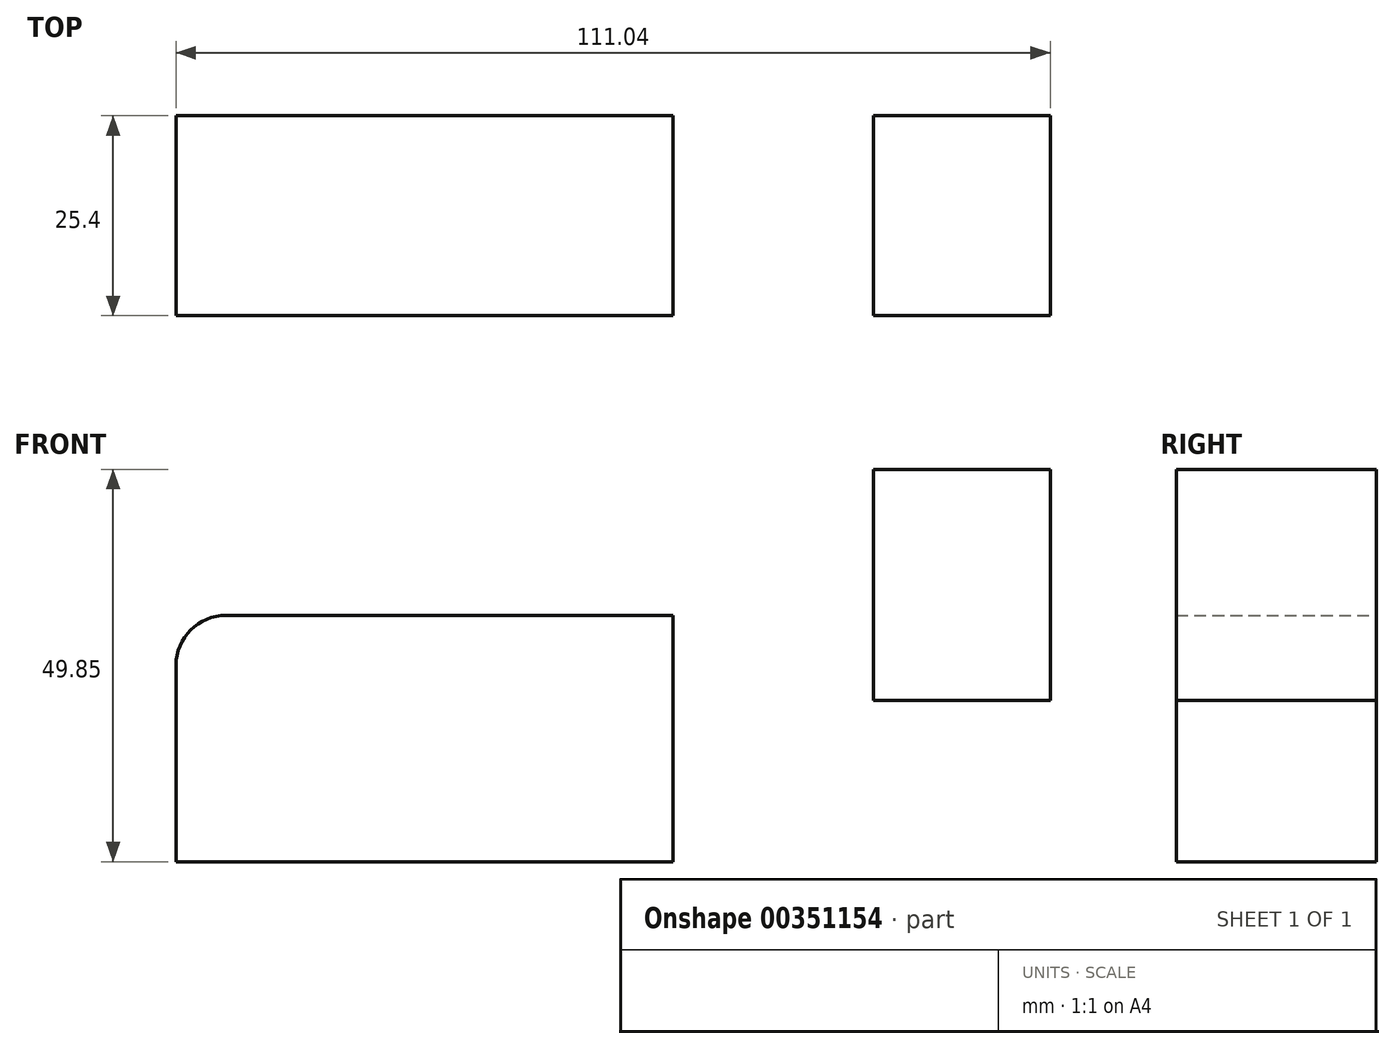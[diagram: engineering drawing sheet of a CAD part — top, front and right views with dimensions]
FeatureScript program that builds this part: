
annotation { "Feature Type Name" : "Feature", "Feature Type Description" : "" }
export const myFeature = defineFeature(function(context is Context, id is Id, definition is map)
    precondition{}
    {
        {
            var Q0;
            Q0=qCreatedBy(makeId("Front.planeOp"),FACE);
            var sketch = newSketch(context, id + "F0", { "sketchPlane" : qUnion([Q0])});
            skLineSegment(sketch, "E0.bottom", {"start": v(31.55, 15.65) * mm, "end": v(-25.2, 15.65) * mm});
            skLineSegment(sketch, "E0.top", {"start": v(31.55, -15.65) * mm, "end": v(-31.55, -15.65) * mm});
            skLineSegment(sketch, "E0.left", {"start": v(31.55, 15.65) * mm, "end": v(31.55, -15.65) * mm});
            skLineSegment(sketch, "E0.right", {"start": v(-31.55, 9.3) * mm, "end": v(-31.55, -15.65) * mm});
            skPoint(sketch, "E0.middle", {"position": v(0, 0) * mm});
            skLineSegment(sketch, "E1.bottom", {"start": v(79.5, 34.2) * mm, "end": v(57.06, 34.2) * mm});
            skLineSegment(sketch, "E1.top", {"start": v(79.5, 4.84) * mm, "end": v(57.06, 4.84) * mm});
            skLineSegment(sketch, "E1.left", {"start": v(79.5, 34.2) * mm, "end": v(79.5, 4.84) * mm});
            skLineSegment(sketch, "E1.right", {"start": v(57.06, 34.2) * mm, "end": v(57.06, 4.84) * mm});
            skPoint(sketch, "E1.middle", {"position": v(68.28, 19.52) * mm});
            skPoint(sketch, "E2.visualSharp", {"position": v(-31.55, 15.65) * mm});
            skArc(sketch, "E2.filletArc", {"start": v(-25.2, 15.65) * mm, "mid": v(-29.7, 13.79) * mm, "end": v(-31.55, 9.3) * mm});
            skSolve(sketch);
        }
        {
            var Q0;
            Q0 = qSketchRegion(id + "F0", true);
            extrude(context, id + "F1", {"entities" : qUnion([Q0]), "depth" : 25.4 * mm});
        }
    });
